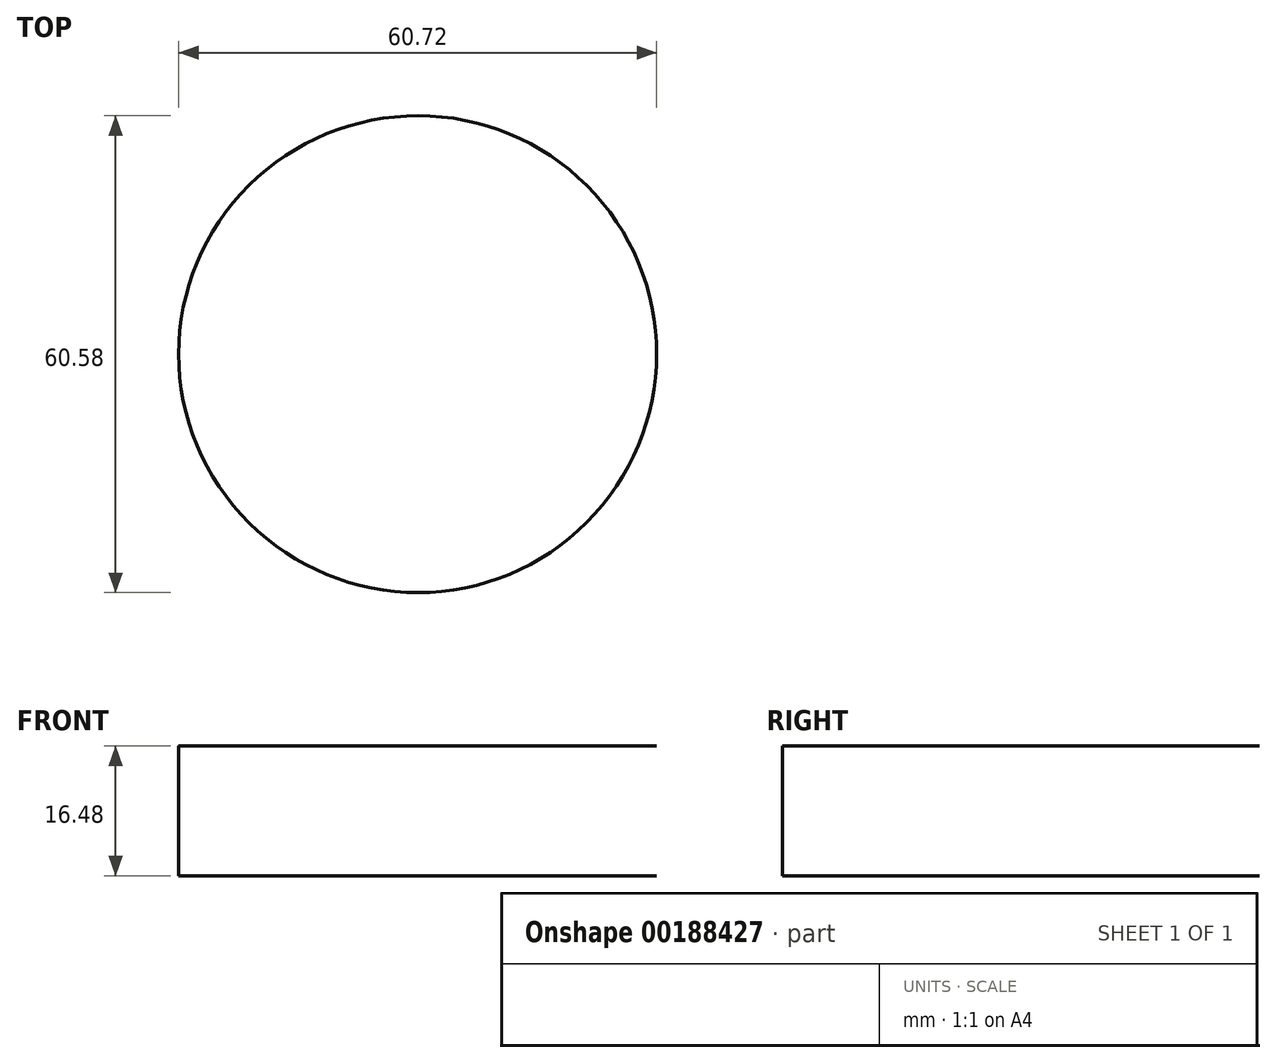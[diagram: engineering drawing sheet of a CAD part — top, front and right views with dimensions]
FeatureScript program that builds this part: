
annotation { "Feature Type Name" : "Feature", "Feature Type Description" : "" }
export const myFeature = defineFeature(function(context is Context, id is Id, definition is map)
    precondition{}
    {
        {
            var Q0;
            Q0=qCreatedBy(makeId("Front.planeOp"),FACE);
            var sketch = newSketch(context, id + "F0", { "sketchPlane" : qUnion([Q0])});
            skArc(sketch, "E0", {"start": v(-24.26, 8.24) * mm, "mid": v(-32.69, 0) * mm, "end": v(-24.27, -8.24) * mm});
            skLineSegment(sketch, "E1", {"start": v(-24.64, 8.24) * mm, "end": v(10.58, 8.24) * mm});
            skLineSegment(sketch, "E2", {"start": v(-24.62, -8.24) * mm, "end": v(10.58, -8.24) * mm});
            skLineSegment(sketch, "E3", {"start": v(10.58, 8.24) * mm, "end": v(10.58, -8.24) * mm});
            skSolve(sketch);
        }
        {
            var Q0;
            {var subQ6=sQuery(id+"F0.wireOp",EDGE,"E3");Q0=makeQuery(id+"F0.imprint","IMPRINT",FACE,{"disambiguationData":[TD([[makeQuery(id+"F0.imprint","IMPRINT",EDGE,{"derivedFrom":subQ6}),-1.0]])]});}
            var Q1;
            Q1=sQuery(id+"F0.wireOp",EDGE,"E3");
            revolve(context, id + "F1", {"entities" : qUnion([Q0]), "axis" : qUnion([Q1]), "revolveType" : RevolveType.FULL});
        }
        {
            var Q0;
            Q0=qCreatedBy(makeId("Top.planeOp"),FACE);
            cPlane(context, id + "F2", {"entities" : qUnion([Q0]), "cplaneType" : CPlaneType.OFFSET, "offset" : 10 * mm, "width" : 152.4 * mm, "height" : 152.4 * mm});
        }
        {
            var Q0;
            Q0=qCreatedBy(id+"F2.planeOp",FACE);
            var sketch = newSketch(context, id + "F3", { "sketchPlane" : qUnion([Q0])});
            skLineSegment(sketch, "E4", {"start": v(8.92, -0.3) * mm, "end": v(3.32, -5.03) * mm});
            skLineSegment(sketch, "E5", {"start": v(3.32, -5.03) * mm, "end": v(10.07, -1.01) * mm});
            skLineSegment(sketch, "E6", {"start": v(10.07, -1.01) * mm, "end": v(8.92, -0.3) * mm});
            skLineSegment(sketch, "E7", {"start": v(10.36, -0.44) * mm, "end": v(10.5, 22.53) * mm});
            skLineSegment(sketch, "E8", {"start": v(10.5, 22.53) * mm, "end": v(9.2, 0.28) * mm});
            skLineSegment(sketch, "E9", {"start": v(9.2, 0.28) * mm, "end": v(10.36, -0.44) * mm});
            skLineSegment(sketch, "E10", {"start": v(11.36, -1.01) * mm, "end": v(29.74, -11.92) * mm});
            skLineSegment(sketch, "E11", {"start": v(29.74, -11.92) * mm, "end": v(12.8, -0.3) * mm});
            skLineSegment(sketch, "E12", {"start": v(12.8, -0.3) * mm, "end": v(11.36, -1.01) * mm});
            skArc(sketch, "E13", {"start": v(-7.44, -23.4) * mm, "mid": v(1.1, -28.3) * mm, "end": v(10.79, -30) * mm});
            skArc(sketch, "E14", {"start": v(10.79, -30) * mm, "mid": v(21.76, -27.8) * mm, "end": v(31.06, -21.57) * mm});
            skArc(sketch, "E15", {"start": v(31.06, -21.57) * mm, "mid": v(37.3, -12.28) * mm, "end": v(39.5, -1.3) * mm});
            skArc(sketch, "E16", {"start": v(39.5, -1.3) * mm, "mid": v(38.99, 3.46) * mm, "end": v(37.7, 8.08) * mm});
            skArc(sketch, "E17", {"start": v(37.7, 8.08) * mm, "mid": v(36.79, 10.3) * mm, "end": v(35.66, 12.4) * mm});
            skArc(sketch, "E18", {"start": v(35.66, 12.4) * mm, "mid": v(34.34, 14.4) * mm, "end": v(32.6, 16.07) * mm});
            skArc(sketch, "E19", {"start": v(32.6, 16.07) * mm, "mid": v(37.09, 7.9) * mm, "end": v(38.64, -1.3) * mm});
            skArc(sketch, "E20", {"start": v(38.64, -1.3) * mm, "mid": v(36.5, -11.95) * mm, "end": v(30.47, -20.98) * mm});
            skArc(sketch, "E21", {"start": v(30.47, -20.98) * mm, "mid": v(21.44, -27.02) * mm, "end": v(10.79, -29.15) * mm});
            skArc(sketch, "E22", {"start": v(10.79, -29.15) * mm, "mid": v(1.16, -27.43) * mm, "end": v(-7.28, -22.5) * mm});
            skArc(sketch, "E23", {"start": v(-7.28, -22.5) * mm, "mid": v(-13.52, -14.97) * mm, "end": v(-16.77, -5.75) * mm});
            skArc(sketch, "E24", {"start": v(-16.77, -5.75) * mm, "mid": v(-13.75, -15.45) * mm, "end": v(-7.44, -23.4) * mm});
            skArc(sketch, "E25", {"start": v(10.79, 27.27) * mm, "mid": v(21.77, 24.98) * mm, "end": v(31.17, 18.86) * mm});
            skArc(sketch, "E26", {"start": v(31.17, 18.86) * mm, "mid": v(37.8, 9.79) * mm, "end": v(40.36, -1.16) * mm});
            skArc(sketch, "E27", {"start": v(40.36, -1.16) * mm, "mid": v(38.14, 10.15) * mm, "end": v(31.7, 19.71) * mm});
            skArc(sketch, "E28", {"start": v(31.7, 19.71) * mm, "mid": v(22.12, 26.15) * mm, "end": v(10.79, 28.41) * mm});
            skArc(sketch, "E29", {"start": v(10.79, 28.41) * mm, "mid": v(-0.6, 26.2) * mm, "end": v(-10.28, 19.81) * mm});
            skArc(sketch, "E30", {"start": v(-10.28, 19.81) * mm, "mid": v(-16.78, 10.21) * mm, "end": v(-19.07, -1.16) * mm});
            skArc(sketch, "E31", {"start": v(-19.07, -1.16) * mm, "mid": v(-16.07, -14.15) * mm, "end": v(-7.73, -24.55) * mm});
            skArc(sketch, "E32", {"start": v(-7.73, -24.55) * mm, "mid": v(-10.15, -21.96) * mm, "end": v(-12.03, -18.95) * mm});
            skArc(sketch, "E33", {"start": v(-12.03, -18.95) * mm, "mid": v(-16.4, -10.53) * mm, "end": v(-17.92, -1.16) * mm});
            skArc(sketch, "E34", {"start": v(-17.92, -1.16) * mm, "mid": v(-15.74, 9.78) * mm, "end": v(-9.5, 19.02) * mm});
            skArc(sketch, "E35", {"start": v(-9.5, 19.02) * mm, "mid": v(-0.16, 25.13) * mm, "end": v(10.79, 27.27) * mm});
            skLineSegment(sketch, "E36", {"start": v(34.33, -14.94) * mm, "end": v(34.47, -14.8) * mm});
            skLineSegment(sketch, "E37", {"start": v(34.47, -14.8) * mm, "end": v(13.8, 0.28) * mm});
            skLineSegment(sketch, "E38", {"start": v(13.8, 0.28) * mm, "end": v(15.67, 1.43) * mm});
            skLineSegment(sketch, "E39", {"start": v(15.67, 1.43) * mm, "end": v(34.62, -14.5) * mm});
            skArc(sketch, "E40", {"start": v(34.62, -14.5) * mm, "mid": v(37.19, -8.12) * mm, "end": v(38.06, -1.3) * mm});
            skArc(sketch, "E41", {"start": v(38.06, -1.3) * mm, "mid": v(36.03, 9.08) * mm, "end": v(30.2, 17.9) * mm});
            skArc(sketch, "E42", {"start": v(30.2, 17.9) * mm, "mid": v(21.43, 23.83) * mm, "end": v(11.08, 25.97) * mm});
            skLineSegment(sketch, "E43", {"start": v(11.08, 25.97) * mm, "end": v(15.24, 2.15) * mm});
            skLineSegment(sketch, "E44", {"start": v(15.24, 2.15) * mm, "end": v(11.08, -0.44) * mm});
            skLineSegment(sketch, "E45", {"start": v(11.08, -0.44) * mm, "end": v(10.79, 25.97) * mm});
            skLineSegment(sketch, "E46", {"start": v(10.79, 25.97) * mm, "end": v(10.5, 25.97) * mm});
            skLineSegment(sketch, "E47", {"start": v(10.5, 25.97) * mm, "end": v(8.06, 1) * mm});
            skLineSegment(sketch, "E48", {"start": v(8.06, 1) * mm, "end": v(6.48, 2) * mm});
            skLineSegment(sketch, "E49", {"start": v(6.48, 2) * mm, "end": v(10.07, 25.97) * mm});
            skArc(sketch, "E50", {"start": v(10.07, 25.97) * mm, "mid": v(-0.18, 23.7) * mm, "end": v(-8.83, 17.76) * mm});
            skArc(sketch, "E51", {"start": v(-8.83, 17.76) * mm, "mid": v(-14.6, 9) * mm, "end": v(-16.63, -1.3) * mm});
            skArc(sketch, "E52", {"start": v(-16.63, -1.3) * mm, "mid": v(-15.74, -8.05) * mm, "end": v(-13.18, -14.36) * mm});
            skLineSegment(sketch, "E53", {"start": v(-13.18, -14.36) * mm, "end": v(5.76, 1.43) * mm});
            skLineSegment(sketch, "E54", {"start": v(5.76, 1.43) * mm, "end": v(7.49, 0.28) * mm});
            skLineSegment(sketch, "E55", {"start": v(7.49, 0.28) * mm, "end": v(-13.04, -14.65) * mm});
            skArc(sketch, "E56", {"start": v(-13.04, -14.65) * mm, "mid": v(-12.93, -14.77) * mm, "end": v(-12.9, -14.94) * mm});
            skLineSegment(sketch, "E57", {"start": v(-12.9, -14.94) * mm, "end": v(10.36, -1.59) * mm});
            skLineSegment(sketch, "E58", {"start": v(10.36, -1.59) * mm, "end": v(10.36, -6.32) * mm});
            skLineSegment(sketch, "E59", {"start": v(10.36, -6.32) * mm, "end": v(-12.6, -15.22) * mm});
            skArc(sketch, "E60", {"start": v(-12.6, -15.22) * mm, "mid": v(-2.68, -25) * mm, "end": v(10.79, -28.57) * mm});
            skArc(sketch, "E61", {"start": v(10.79, -28.57) * mm, "mid": v(24.26, -25) * mm, "end": v(34.19, -15.22) * mm});
            skLineSegment(sketch, "E62", {"start": v(34.19, -15.22) * mm, "end": v(11.08, -6.32) * mm});
            skLineSegment(sketch, "E63", {"start": v(11.08, -6.32) * mm, "end": v(11.08, -1.59) * mm});
            skLineSegment(sketch, "E64", {"start": v(11.08, -1.59) * mm, "end": v(34.47, -14.8) * mm});
            skLineSegment(sketch, "E65", {"start": v(34.47, -14.8) * mm, "end": v(34.33, -14.94) * mm});
            skArc(sketch, "E66", {"start": v(10.79, 28.99) * mm, "mid": v(-0.83, 26.7) * mm, "end": v(-10.72, 20.15) * mm});
            skArc(sketch, "E67", {"start": v(-10.72, 20.15) * mm, "mid": v(-17.32, 10.32) * mm, "end": v(-19.64, -1.3) * mm});
            skArc(sketch, "E68", {"start": v(-19.64, -1.3) * mm, "mid": v(-17.31, -12.91) * mm, "end": v(-10.69, -22.72) * mm});
            skArc(sketch, "E69", {"start": v(-10.69, -22.72) * mm, "mid": v(-0.83, -29.28) * mm, "end": v(10.79, -31.59) * mm});
            skArc(sketch, "E70", {"start": v(10.79, -31.59) * mm, "mid": v(22.37, -29.27) * mm, "end": v(32.18, -22.69) * mm});
            skArc(sketch, "E71", {"start": v(32.18, -22.69) * mm, "mid": v(38.75, -12.87) * mm, "end": v(41.08, -1.3) * mm});
            skArc(sketch, "E72", {"start": v(41.08, -1.3) * mm, "mid": v(38.77, 10.3) * mm, "end": v(32.2, 20.12) * mm});
            skArc(sketch, "E73", {"start": v(32.2, 20.12) * mm, "mid": v(22.38, 26.68) * mm, "end": v(10.79, 28.99) * mm});
            skLineSegment(sketch, "E74", {"start": v(-210.9, 99.1) * mm, "end": v(-210.9, -99.1) * mm});
            skLineSegment(sketch, "E75", {"start": v(-210.9, -99.1) * mm, "end": v(210.9, -99.1) * mm});
            skLineSegment(sketch, "E76", {"start": v(210.9, -99.1) * mm, "end": v(210.9, 99.1) * mm});
            skLineSegment(sketch, "E77", {"start": v(210.9, 99.1) * mm, "end": v(-210.9, 99.1) * mm});
            skSolve(sketch);
        }
        {
            var Q0;
            Q0 = qSketchRegion(id + "F3", true);
            extrude(context, id + "F4", {"entities" : qUnion([Q0]), "operationType" : NewBodyOperationType.REMOVE, "oppositeDirection" : true, "depth" : 25.4 * mm});
        }
    });
